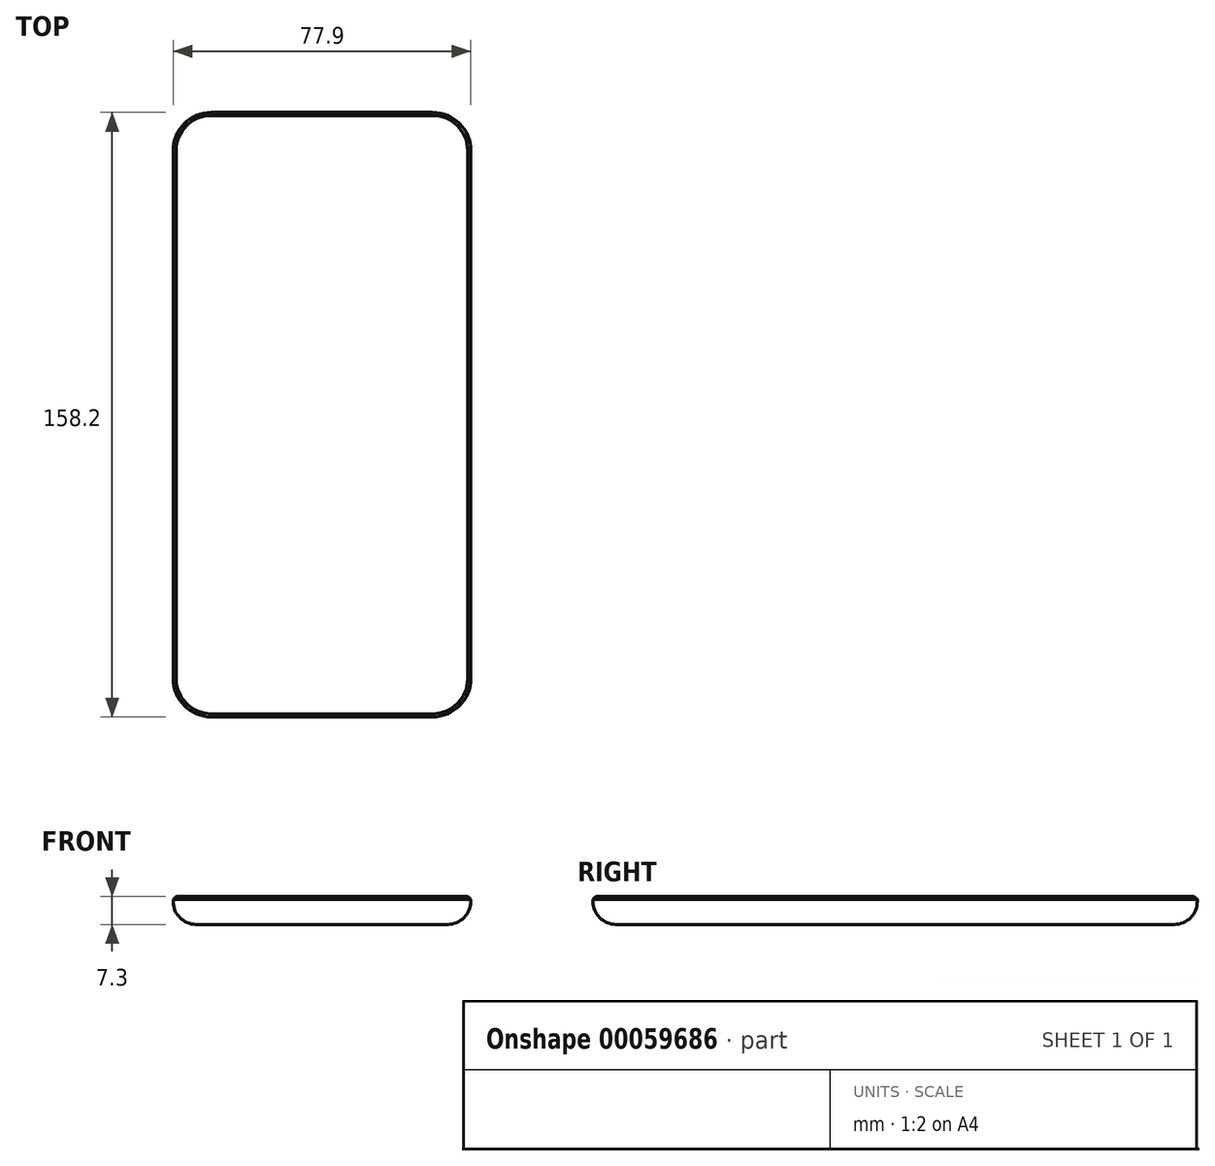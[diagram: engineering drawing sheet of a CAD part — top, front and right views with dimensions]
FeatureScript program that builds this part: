
annotation { "Feature Type Name" : "Feature", "Feature Type Description" : "" }
export const myFeature = defineFeature(function(context is Context, id is Id, definition is map)
    precondition{}
    {
        {
            var Q0;
            Q0=qCreatedBy(makeId("Top.planeOp"),FACE);
            var sketch = newSketch(context, id + "F0", { "sketchPlane" : qUnion([Q0])});
            skLineSegment(sketch, "E0.rect.bottom", {"start": v(38.95, 79.1) * mm, "end": v(-38.95, 79.1) * mm, "construction": true});
            skLineSegment(sketch, "E0.rect.top", {"start": v(38.95, -79.1) * mm, "end": v(-38.95, -79.1) * mm, "construction": true});
            skLineSegment(sketch, "E0.rect.left", {"start": v(38.95, 79.1) * mm, "end": v(38.95, -79.1) * mm, "construction": true});
            skLineSegment(sketch, "E0.rect.right", {"start": v(-38.95, 79.1) * mm, "end": v(-38.95, -79.1) * mm, "construction": true});
            skPoint(sketch, "E0.rect.middle", {"position": v(0, 0) * mm});
            skArc(sketch, "E1", {"start": v(-28.95, 79.1) * mm, "mid": v(-36.02, 76.17) * mm, "end": v(-38.95, 69.1) * mm});
            skArc(sketch, "E2", {"start": v(38.95, 69.1) * mm, "mid": v(36.02, 76.17) * mm, "end": v(28.95, 79.1) * mm});
            skArc(sketch, "E3", {"start": v(-38.95, -69.1) * mm, "mid": v(-36.02, -76.17) * mm, "end": v(-28.95, -79.1) * mm});
            skArc(sketch, "E4", {"start": v(28.95, -79.1) * mm, "mid": v(36.02, -76.17) * mm, "end": v(38.95, -69.1) * mm});
            skLineSegment(sketch, "E5", {"start": v(-28.95, 79.1) * mm, "end": v(28.95, 79.1) * mm});
            skLineSegment(sketch, "E6", {"start": v(38.95, 69.1) * mm, "end": v(38.95, -69.1) * mm});
            skLineSegment(sketch, "E7", {"start": v(-28.95, -79.1) * mm, "end": v(28.95, -79.1) * mm});
            skLineSegment(sketch, "E8", {"start": v(-38.95, 69.1) * mm, "end": v(-38.95, -69.1) * mm});
            skSolve(sketch);
        }
        {
            var Q0;
            Q0 = qSketchRegion(id + "F0", true);
            extrude(context, id + "F1", {"entities" : qUnion([Q0]), "depth" : 7.3 * mm});
        }
        {
            var Q0;
            Q0=makeQuery(id+"F1.opExtrude","CAP_FACE",FACE,{"disambiguationData":[OSD([sQuery(id+"F0.wireOp",EDGE,"E1"),sQuery(id+"F0.wireOp",EDGE,"E2"),sQuery(id+"F0.wireOp",EDGE,"E3"),sQuery(id+"F0.wireOp",EDGE,"E4"),sQuery(id+"F0.wireOp",EDGE,"E5"),sQuery(id+"F0.wireOp",EDGE,"E6"),sQuery(id+"F0.wireOp",EDGE,"E7"),sQuery(id+"F0.wireOp",EDGE,"E8")])],"isStart":true});
            fillet(context, id + "F2", {"entities" : qUnion([Q0]), "radius" : 6 * mm, "tangentPropagation" : true, "allowEdgeOverflow" : false});
        }
        {
            var Q0;
            Q0=makeQuery(id+"F1.opExtrude","CAP_FACE",FACE,{"disambiguationData":[OSD([sQuery(id+"F0.wireOp",EDGE,"E1"),sQuery(id+"F0.wireOp",EDGE,"E2"),sQuery(id+"F0.wireOp",EDGE,"E3"),sQuery(id+"F0.wireOp",EDGE,"E4"),sQuery(id+"F0.wireOp",EDGE,"E5"),sQuery(id+"F0.wireOp",EDGE,"E6"),sQuery(id+"F0.wireOp",EDGE,"E7"),sQuery(id+"F0.wireOp",EDGE,"E8")])],"isStart":false});
            chamfer(context, id + "F3", {"entities" : qUnion([Q0]), "width" : .8 * mm, "tangentPropagation" : true});
        }
    });
